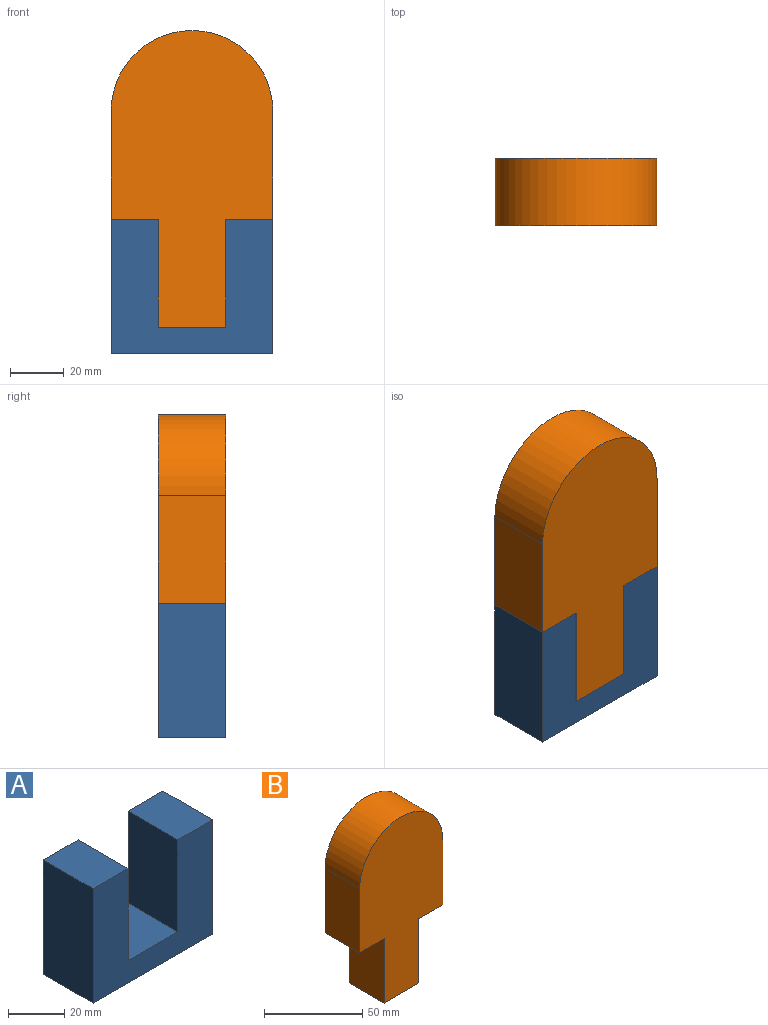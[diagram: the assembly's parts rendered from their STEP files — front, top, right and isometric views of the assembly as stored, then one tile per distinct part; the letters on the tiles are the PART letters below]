
ASSEMBLY  parts=2 mates=1
PART A: 10 faces, bbox 60x25x49.7 mm
  f0: plane 25x17.5mm, normal (0,0,1), area 437.5mm2, adj f1,f7,f8,f9
  f1: plane 49.72x25mm, normal (-1,0,0), area 1243.1mm2, adj f0,f2,f8,f9
  f2: plane 60x25mm, normal (0,0,-1), area 1500mm2, adj f1,f3,f8,f9
  f3: plane 49.72x25mm, normal (1,0,0), area 1243.1mm2, adj f2,f4,f8,f9
  f4: plane 25x17.5mm, normal (0,0,1), area 437.5mm2, adj f3,f5,f8,f9
  f5: plane 40x25mm, normal (-1,0,0), area 1000mm2, adj f4,f6,f8,f9
  f6: plane 25x25mm, normal (0,0,1), area 625mm2, adj f5,f7,f8,f9
  f7: plane 40x25mm, normal (1,0,0), area 1000mm2, adj f0,f6,f8,f9
  f8: plane 60x49.72mm, normal (0,-1,0), area 1983.3mm2, adj f0,f1,f2,f3,f4,f5,f6,f7
  f9: plane 60x49.72mm, normal (0,1,0), area 1983.3mm2, adj f0,f1,f2,f3,f4,f5,f6,f7
PART B: 10 faces, bbox 60x25x110 mm
  f0: cylinder r=30mm len=60mm, axis (0,1,0), area 2356.2mm2, adj f1,f7,f8,f9
  f1: plane 40x25mm, normal (-1,0,0), area 1000mm2, adj f0,f2,f8,f9
  f2: plane 25x17.5mm, normal (0,0,-1), area 437.5mm2, adj f1,f3,f8,f9
  f3: plane 40x25mm, normal (-1,0,0), area 1000mm2, adj f2,f4,f8,f9
  f4: plane 25x25mm, normal (0,0,-1), area 625mm2, adj f3,f5,f8,f9
  f5: plane 40x25mm, normal (1,0,0), area 1000mm2, adj f4,f6,f8,f9
  f6: plane 25x17.5mm, normal (0,0,-1), area 437.5mm2, adj f5,f7,f8,f9
  f7: plane 40x25mm, normal (1,0,0), area 1000mm2, adj f0,f6,f8,f9
  f8: plane 110x60mm, normal (0,-1,0), area 4813.7mm2, adj f0,f1,f2,f3,f4,f5,f6,f7
  f9: plane 110x60mm, normal (0,1,0), area 4813.7mm2, adj f0,f1,f2,f3,f4,f5,f6,f7
PLACE A t=(20.98,41.83,-26.63)mm
PLACE B t=(15.59,41.83,22.68)mm
MATE fastened A.f6 <-> B.f4  axis (0,0,1) through (16.54,41.83,-39.7)mm
